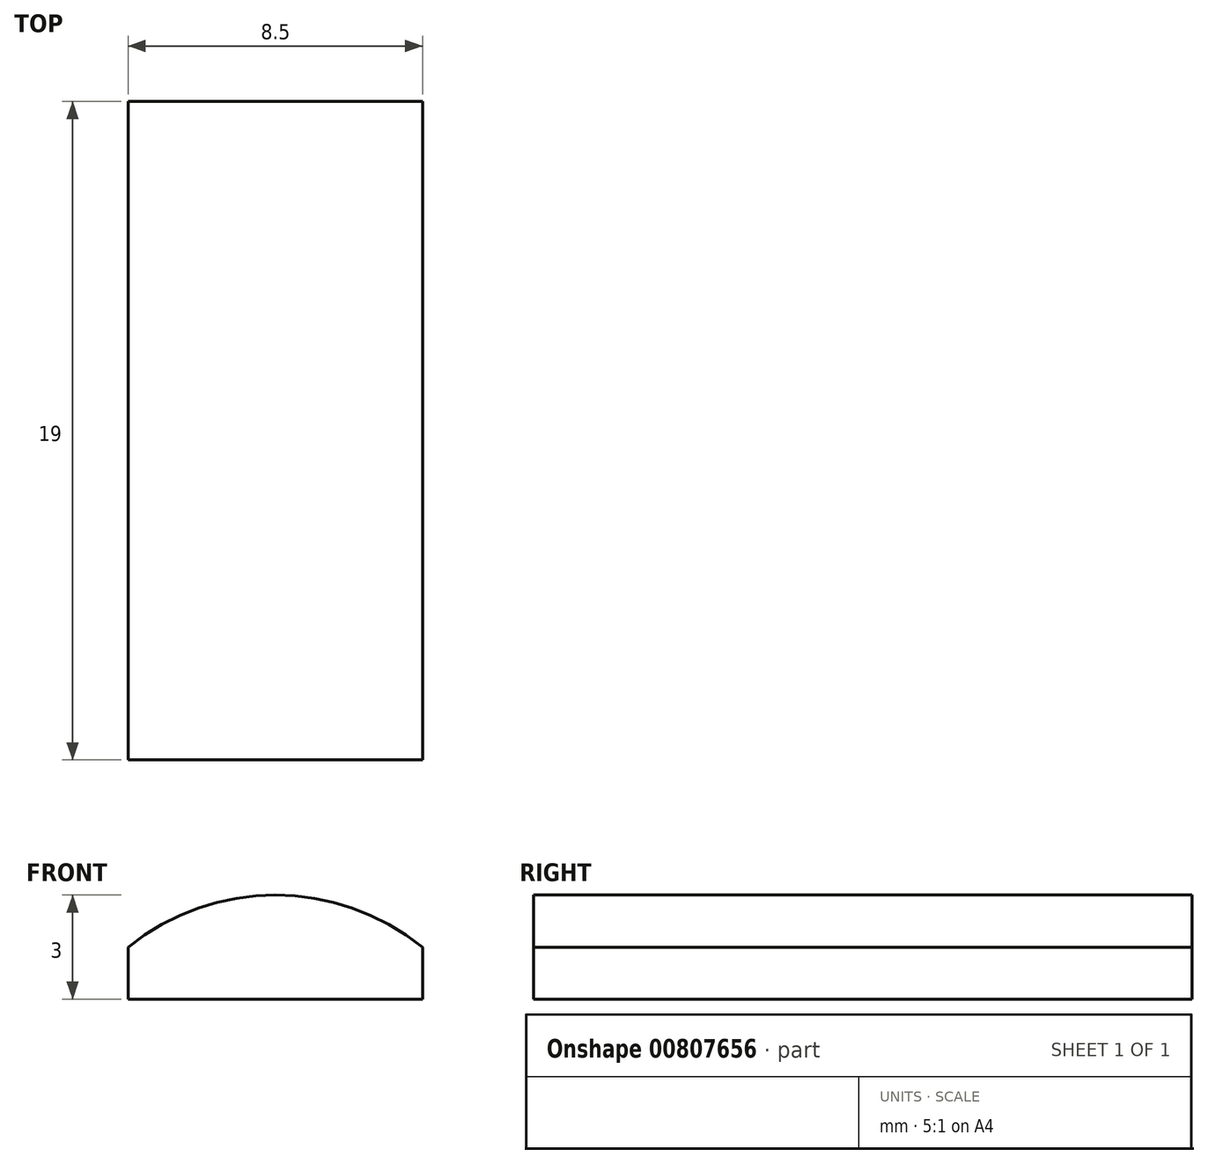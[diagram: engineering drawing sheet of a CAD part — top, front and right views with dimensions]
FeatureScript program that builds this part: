
annotation { "Feature Type Name" : "Feature", "Feature Type Description" : "" }
export const myFeature = defineFeature(function(context is Context, id is Id, definition is map)
    precondition{}
    {
        {
            var Q0;
            Q0=qCreatedBy(makeId("Top.planeOp"),FACE);
            var sketch = newSketch(context, id + "F0", { "sketchPlane" : qUnion([Q0])});
            skLineSegment(sketch, "E0.bottom", {"start": v(4.25, -9.5) * mm, "end": v(-4.25, -9.5) * mm});
            skLineSegment(sketch, "E0.top", {"start": v(4.25, 9.5) * mm, "end": v(-4.25, 9.5) * mm});
            skLineSegment(sketch, "E0.left", {"start": v(4.25, -9.5) * mm, "end": v(4.25, 9.5) * mm});
            skLineSegment(sketch, "E0.right", {"start": v(-4.25, -9.5) * mm, "end": v(-4.25, 9.5) * mm});
            skPoint(sketch, "E0.middle", {"position": v(0, 0) * mm});
            skSolve(sketch);
        }
        {
            var Q0;
            Q0=makeQuery(id+"F0.imprint","IMPRINT",FACE,{"disambiguationData":[TD([[makeQuery(id+"F0.imprint","IMPRINT",EDGE,{"derivedFrom":sQuery(id+"F0.wireOp",EDGE,"E0.bottom")}),-1.0]])]});
            extrude(context, id + "F1", {"entities" : qUnion([Q0]), "depth" : 3 * mm, "offsetDistance" : 25 * mm});
        }
        {
            var Q0;
            Q0=makeQuery(id+"F1.opExtrude","SWEPT_FACE",FACE,{"disambiguationData":[OSD([sQuery(id+"F0.wireOp",EDGE,"E0.top")])]});
            var sketch = newSketch(context, id + "F2", { "sketchPlane" : qUnion([Q0])});
            skPoint(sketch, "E1", {"position": v(0, 3) * mm});
            skLineSegment(sketch, "E2", {"start": v(-4.25, 0) * mm, "end": v(-4.25, 1.5) * mm});
            skLineSegment(sketch, "E3.MirrorCS", {"start": v(4.25, 0) * mm, "end": v(4.25, 1.5) * mm});
            skArc(sketch, "E4", {"start": v(4.25, 1.5) * mm, "mid": v(0, 3) * mm, "end": v(-4.25, 1.5) * mm});
            skSolve(sketch);
        }
        {
            var Q0;
            {var subQ0=sQuery(id+"F2.wireOp",EDGE,"E4");var subQ1=sQuery(id+"F0.wireOp",EDGE,"E0.top");var subQ4=makeQuery(id+"F1.opExtrude","CAP_EDGE",EDGE,{"disambiguationData":[OSD([subQ1])],"isStart":false});var subQ5=makeQuery(id+"F2.imprint","INTERSECT",VERTEX,{"derivedFrom":[subQ4,subQ0]});Q0=makeQuery(id+"F2.imprint","IMPRINT",FACE,{"disambiguationData":[TD([[makeQuery(id+"F2.imprint","IMPRINT",EDGE,{"disambiguationData":[TD([[subQ5,1.0]])],"derivedFrom":subQ4}),-1.0]])]});}
            var Q1;
            {var subQ0=sQuery(id+"F2.wireOp",EDGE,"E4");var subQ1=sQuery(id+"F0.wireOp",EDGE,"E0.top");var subQ4=makeQuery(id+"F1.opExtrude","CAP_EDGE",EDGE,{"disambiguationData":[OSD([subQ1])],"isStart":false});var subQ5=makeQuery(id+"F2.imprint","INTERSECT",VERTEX,{"derivedFrom":[subQ4,subQ0]});Q1=makeQuery(id+"F2.imprint","IMPRINT",FACE,{"disambiguationData":[TD([[makeQuery(id+"F2.imprint","IMPRINT",EDGE,{"disambiguationData":[TD([[subQ5,-1.0]])],"derivedFrom":subQ4}),-1.0]])]});}
            extrude(context, id + "F3", {"entities" : qUnion([Q0, Q1]), "operationType" : NewBodyOperationType.REMOVE, "oppositeDirection" : true, "depth" : 25 * mm, "offsetDistance" : 25 * mm});
        }
    });
